# Revit family: PRD_FrankeWS_Mrrs_Heavy-DutyMirror_M400HD-M600HD
name_source: partatom
category: Furniture
revit_build: Autodesk Revit 2018 (Build: 20190510_1515(x64)
units: mm (PartAtom-declared; Revit-internal decimal feet)

## family parameters
Cut with Voids When Loaded = No
Host = Face
OmniClass Number = 23.40.20.21
OmniClass Title = Toilet and Bath Specialties
Room Calculation Point = No
Shared = No

## types (3) — shared parameters
AssetType = Fixed
Category = Pr_25_71_53_06, Bathroom mirrors
Color = Stainless steel
Default Elevation = 1100 mm
DurationUnit = year
Finish = High polished
Form = Wall mounted
IfcExportAs = IfcFurnitureType
IfcExportType = NOTDEFINED
IntegralAccessories = Stainless steel screws and dowels incl.
MainColor = Stainless steel
Manufacturer = KWC Group AG
ManufacturerName = KWC Group AG
ManufacturerURL = www.kwc.com
Material = Stainless steel
MaterialsFrame = Polystyrene
MaterialsGlazing = Stainless steel 1.4301
MirrorMaterial = PRD_AR_StainlessSteel_HighPolished
NBSDescription = Mirrors
NBSReference = 45-35-72/336
NominalDepth = 8 mm  [stored 0.0262467 ft]
ProductInformation = https://pim.kwc.com
TypeOfFixing = Catch
URL = www.kwc.com
Uniclass2015Code = Pr_25_71_53_06
Uniclass2015Title = Bathroom mirrors
Uniclass2015Version = Products v1.5
Version = 1
WarrantyDurationUnit = year

## per-type parameters (varying)
| type | BIMObjectName | Description | Features | GrossWeight | Model | ModelNumber | ModelReference | Name | NetWeight | NominalHeight | NominalLength | NominalWidth | Size |
| M400HD, 390 x 290 mm | PRD_AR_Mirrors_Heavy-DutyMirror_M400HD | Stainless steel mirror for wall mounting, mirror with a reflective polished surface, material thickness 1 mm, hidden thief resistant fixings, reinforced with polystyrene plate, incl. stainless steel screws and dowels. size: 390 x 290 mm | Mirror with reinforcement plate, stainless steel, 1.00 mm, high polished, wall mounting, 390x290x8 mm (WxHxD) | 3.10 kg | M400HD | 2000057089 | M400HD | HEAVY-DUTY mirror M400HD | 2.80 kg | 290 mm  [stored 0.951444 ft] | 390 mm  [stored 1.27953 ft] | 390 mm  [stored 1.27953 ft] | 390 x 290 x 8 mm |
| M500HD, 490 x 390 mm | PRD_AR_Mirrors_Heavy-DutyMirror_M500HD | Stainless steel mirror for wall mounting, mirror with a reflective polished surface, material thickness 1 mm, hidden thief resistant fixings, reinforced with polystyrene plate, incl. stainless steel screws and dowels. size: 490 x 390 mm | Mirror with reinforcement plate, stainless steel, 1.00 mm, high polished, wall mounting, 490x390x8 mm (WxHxD) | 3.90 kg | M500HD | 2000057090 | M500HD | HEAVY-DUTY mirror M500HD | 3.50 kg | 390 mm  [stored 1.27953 ft] | 490 mm  [stored 1.60761 ft] | 490 mm  [stored 1.60761 ft] | 490 x 390 x 8 mm |
| M600HD, 590 x 490 mm | PRD_AR_Mirrors_Heavy-DutyMirror_M600HD | Stainless steel mirror for wall mounting, mirror with a reflective polished surface, material thickness 1 mm, hidden thief resistant fixings, reinforced with polystyrene plate, incl. stainless steel screws and dowels. size: 590 x 490 mm | Mirror with reinforcement plate, stainless steel, 1.00 mm, high polished, wall mounting, 590x490x8 mm (WxHxD) | 4.40 kg | M600HD | 2000057091 | M600HD | HEAVY-DUTY mirror M600HD | 4.00 kg | 490 mm  [stored 1.60761 ft] | 590 mm  [stored 1.9357 ft] | 590 mm  [stored 1.9357 ft] | 590 x 490 x 8 mm |

note: [stored X ft] marks values corroborated as IEEE doubles in the binary element streams (Revit-internal decimal feet)

## geometry (parser evidence)
native form markers: Sweep x2
no freeform markers — native parametric forms only
